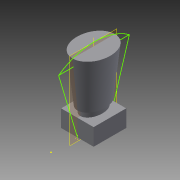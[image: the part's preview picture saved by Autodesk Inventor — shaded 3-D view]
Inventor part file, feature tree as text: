
AUTODESK INVENTOR PART (.ipt)
format: ipt  version: 2015 (Build 190159000, 159)  size: 153,600 bytes
history: native  units: in
note: dims shown in document units (in); Inventor stores cm internally (conversion verified against a paired STEP export)
features: sketch x4, extrude x3, other x1, plane x1
ambient origin geometry x8: Origin, YZ Plane, XZ Plane, XY Plane, X Axis, Y Axis, Z Axis, Center Point
bodies: Solid1 (feature_tree)
feature tree (9):
  extrude  "Extrusion1"  Depth=0.575in
  sketch  "Sketch3"  dims[d2=0.3in d3=0.0in d13=0.236in]
  extrude  "Extrusion3"  Depth=0.236in
  extrude  "Extrusion4"  Depth=0.205in
  other  "Work Axis1"
  plane  "Work Plane2"
  sketch  "Sketch9"  dims[d16=0.286in d19=0.11in d20=0.0in d21=0.84in d22=0.0412in]
  sketch  "Sketch2"  dims[d0=0.575in d1=0.575in]
  sketch  "Sketch6"  dims[d14=0.155in d15=0.205in]
